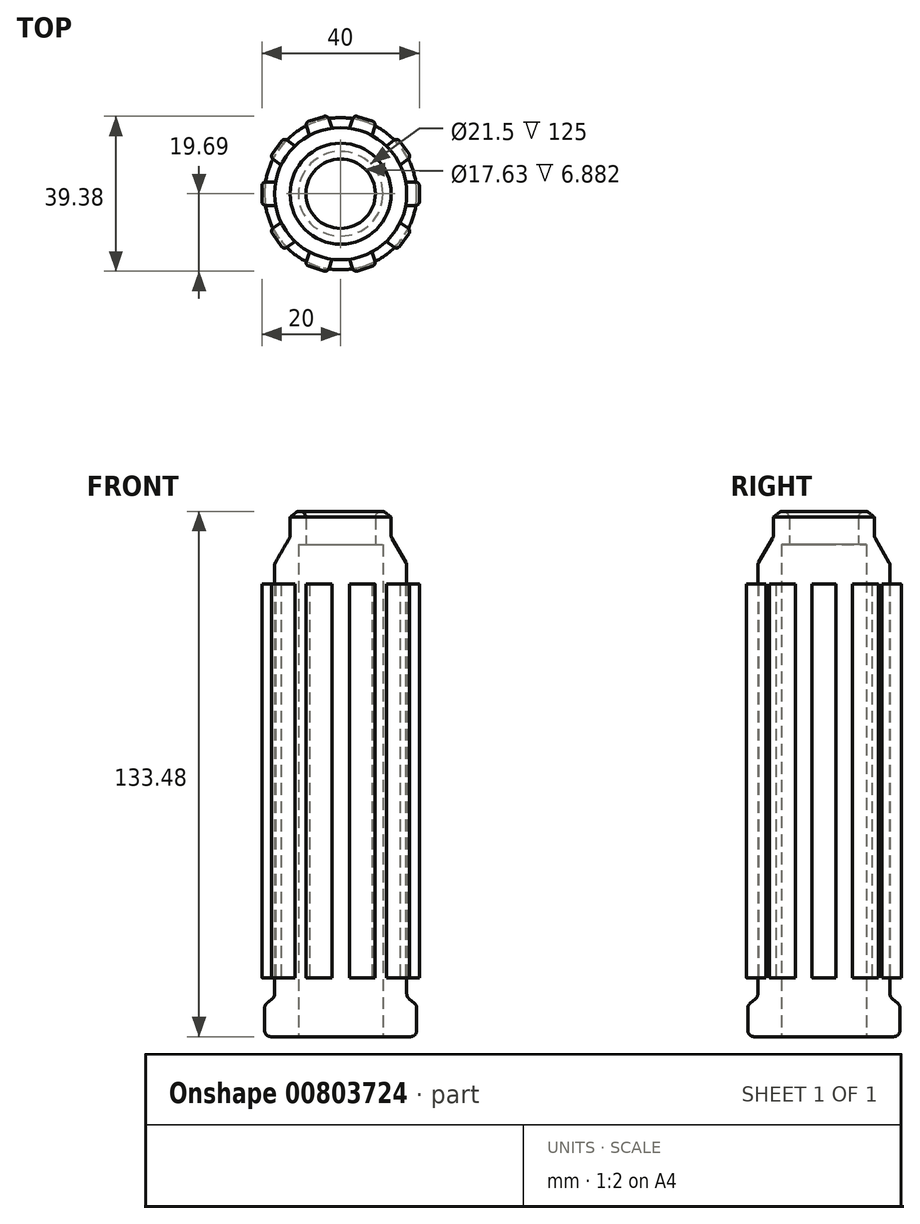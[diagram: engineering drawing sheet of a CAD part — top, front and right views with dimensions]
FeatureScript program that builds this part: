
annotation { "Feature Type Name" : "Feature", "Feature Type Description" : "" }
export const myFeature = defineFeature(function(context is Context, id is Id, definition is map)
    precondition{}
    {
        {
            var Q0;
            Q0=qCreatedBy(makeId("Front.planeOp"),FACE);
            var sketch = newSketch(context, id + "F0", { "sketchPlane" : qUnion([Q0])});
            skLineSegment(sketch, "E0", {"start": v(0, 0) * mm, "end": v(0, 36.36) * mm, "construction": true});
            skLineSegment(sketch, "E1", {"start": v(10.75, 0) * mm, "end": v(10.75, 125) * mm});
            skLineSegment(sketch, "E2", {"start": v(10.75, 125) * mm, "end": v(8.82, 125) * mm});
            skLineSegment(sketch, "E3", {"start": v(8.82, 125) * mm, "end": v(8.82, 135) * mm});
            skArc(sketch, "E4", {"start": v(12.82, 132) * mm, "mid": v(10.86, 133.56) * mm, "end": v(8.82, 135) * mm});
            skLineSegment(sketch, "E5", {"start": v(12.82, 132) * mm, "end": v(12.82, 127) * mm});
            skLineSegment(sketch, "E6", {"start": v(12.82, 127) * mm, "end": v(16.79, 120.13) * mm});
            skLineSegment(sketch, "E7", {"start": v(16.79, 120.13) * mm, "end": v(16.79, 10.13) * mm});
            skLineSegment(sketch, "E8", {"start": v(16.79, 10.13) * mm, "end": v(19.32, 8) * mm});
            skLineSegment(sketch, "E9", {"start": v(19.33, 8) * mm, "end": v(19.33, 0) * mm});
            skLineSegment(sketch, "E10", {"start": v(19.33, 0) * mm, "end": v(10.75, 0) * mm});
            skSolve(sketch);
        }
        {
            var Q0;
            Q0=makeQuery(id+"F0.imprint","IMPRINT",FACE,{"disambiguationData":[TD([[makeQuery(id+"F0.imprint","IMPRINT",EDGE,{"derivedFrom":sQuery(id+"F0.wireOp",EDGE,"E1")}),-1.0]])]});
            var Q1;
            Q1=sQuery(id+"F0.wireOp",EDGE,"E0");
            revolve(context, id + "F1", {"surfaceOperationType" : NewSurfaceOperationType.NEW, "entities" : qUnion([Q0]), "axis" : qUnion([Q1]), "revolveType" : RevolveType.FULL});
        }
        {
            var Q0;
            Q0=makeQuery(id+"F1.opRevolve","SWEPT_EDGE",EDGE,{"disambiguationData":[OSD([sQuery(id+"F0.wireOp",EDGE,"E3"),sQuery(id+"F0.wireOp",EDGE,"E4")])]});
            var Q1;
            Q1=makeQuery(id+"F1.opRevolve","SWEPT_EDGE",EDGE,{"disambiguationData":[OSD([sQuery(id+"F0.wireOp",EDGE,"E5"),sQuery(id+"F0.wireOp",EDGE,"E6")])]});
            var Q2;
            Q2=makeQuery(id+"F1.opRevolve","SWEPT_EDGE",EDGE,{"disambiguationData":[OSD([sQuery(id+"F0.wireOp",EDGE,"E6"),sQuery(id+"F0.wireOp",EDGE,"E7")])]});
            var Q3;
            Q3=makeQuery(id+"F1.opRevolve","SWEPT_EDGE",EDGE,{"disambiguationData":[OSD([sQuery(id+"F0.wireOp",EDGE,"E7"),sQuery(id+"F0.wireOp",EDGE,"E8")])]});
            var Q4;
            Q4=makeQuery(id+"F1.opRevolve","SWEPT_EDGE",EDGE,{"disambiguationData":[OSD([sQuery(id+"F0.wireOp",EDGE,"E8"),sQuery(id+"F0.wireOp",EDGE,"E9")])]});
            var Q5;
            Q5=makeQuery(id+"F1.opRevolve","SWEPT_EDGE",EDGE,{"disambiguationData":[OSD([sQuery(id+"F0.wireOp",EDGE,"E9"),sQuery(id+"F0.wireOp",EDGE,"E10")])]});
            fillet(context, id + "F2", {"entities" : qUnion([Q0, Q1, Q2, Q3, Q4, Q5]), "radius" : 1.6 * mm, "tangentPropagation" : true, "allowEdgeOverflow" : false});
        }
        {
            var Q0;
            Q0=qCreatedBy(makeId("Right.planeOp"),FACE);
            cPlane(context, id + "F3", {"entities" : qUnion([Q0]), "cplaneType" : CPlaneType.OFFSET, "offset" : 20 * mm, "width" : 150 * mm, "height" : 150 * mm});
        }
        {
            var Q0;
            Q0=qCreatedBy(id+"F3.planeOp",FACE);
            var sketch = newSketch(context, id + "F4", { "sketchPlane" : qUnion([Q0])});
            skLineSegment(sketch, "E11.bottom", {"start": v(-3, 115) * mm, "end": v(3, 115) * mm});
            skLineSegment(sketch, "E11.top", {"start": v(-3, 15) * mm, "end": v(3, 15) * mm});
            skLineSegment(sketch, "E11.left", {"start": v(-3, 115) * mm, "end": v(-3, 15) * mm});
            skLineSegment(sketch, "E11.right", {"start": v(3, 115) * mm, "end": v(3, 15) * mm});
            skSolve(sketch);
        }
        {
            var Q0;
            Q0=makeQuery(id+"F4.imprint","IMPRINT",FACE,{"disambiguationData":[TD([[makeQuery(id+"F4.imprint","IMPRINT",EDGE,{"derivedFrom":sQuery(id+"F4.wireOp",EDGE,"E11.bottom")}),-1.0]])]});
            var Q1;
            Q1=makeQuery(id+"F1.opRevolve","SWEPT_FACE",FACE,{"disambiguationData":[OSD([sQuery(id+"F0.wireOp",EDGE,"E7")])]});
            extrude(context, id + "F5", {"entities" : qUnion([Q0]), "endBound" : BoundingType.UP_TO_SURFACE, "oppositeDirection" : true, "depth" : 25 * mm, "endBoundEntityFace" : qUnion([Q1]), "offsetDistance" : 25 * mm});
        }
        {
            var Q0;
            Q0=makeQuery(id+"F5.opExtrude","CAP_EDGE",EDGE,{"disambiguationData":[OSD([sQuery(id+"F4.wireOp",EDGE,"E11.left")])],"isStart":true});
            var Q1;
            Q1=makeQuery(id+"F5.opExtrude","CAP_EDGE",EDGE,{"disambiguationData":[OSD([sQuery(id+"F4.wireOp",EDGE,"E11.right")])],"isStart":true});
            fillet(context, id + "F6", {"entities" : qUnion([Q0, Q1]), "radius" : 1 * mm, "tangentPropagation" : true, "allowEdgeOverflow" : false});
        }
        {
            var Q0;
            Q0=makeQuery(id+"F5.opExtrude","SWEPT_BODY",BODY,{"disambiguationData":[OSD([sQuery(id+"F4.wireOp",EDGE,"E11.bottom"),sQuery(id+"F4.wireOp",EDGE,"E11.top"),sQuery(id+"F4.wireOp",EDGE,"E11.left"),sQuery(id+"F4.wireOp",EDGE,"E11.right")])]});
            var Q1;
            {var subQ0=sQuery(id+"F0.wireOp",EDGE,"E8");Q1=makeQuery(id+"F2.opFillet","BLEND_EDGE",EDGE,{"blendedFrom":[makeQuery(id+"F1.opRevolve","SWEPT_EDGE",EDGE,{"disambiguationData":[OSD([sQuery(id+"F0.wireOp",EDGE,"E7"),subQ0])]}),makeQuery(id+"F1.opRevolve","SWEPT_FACE",FACE,{"disambiguationData":[OSD([subQ0])]})],"blendedInto":[makeQuery(id+"F1.opRevolve","SWEPT_FACE",FACE,{"disambiguationData":[OSD([subQ0])]})]});}
            circularPattern(context, id + "F7", {"entities" : qUnion([Q0]), "axis" : qUnion([Q1]), "angle" : 360 * degree, "instanceCount" : 10, "equalSpace" : true});
        }
    });
